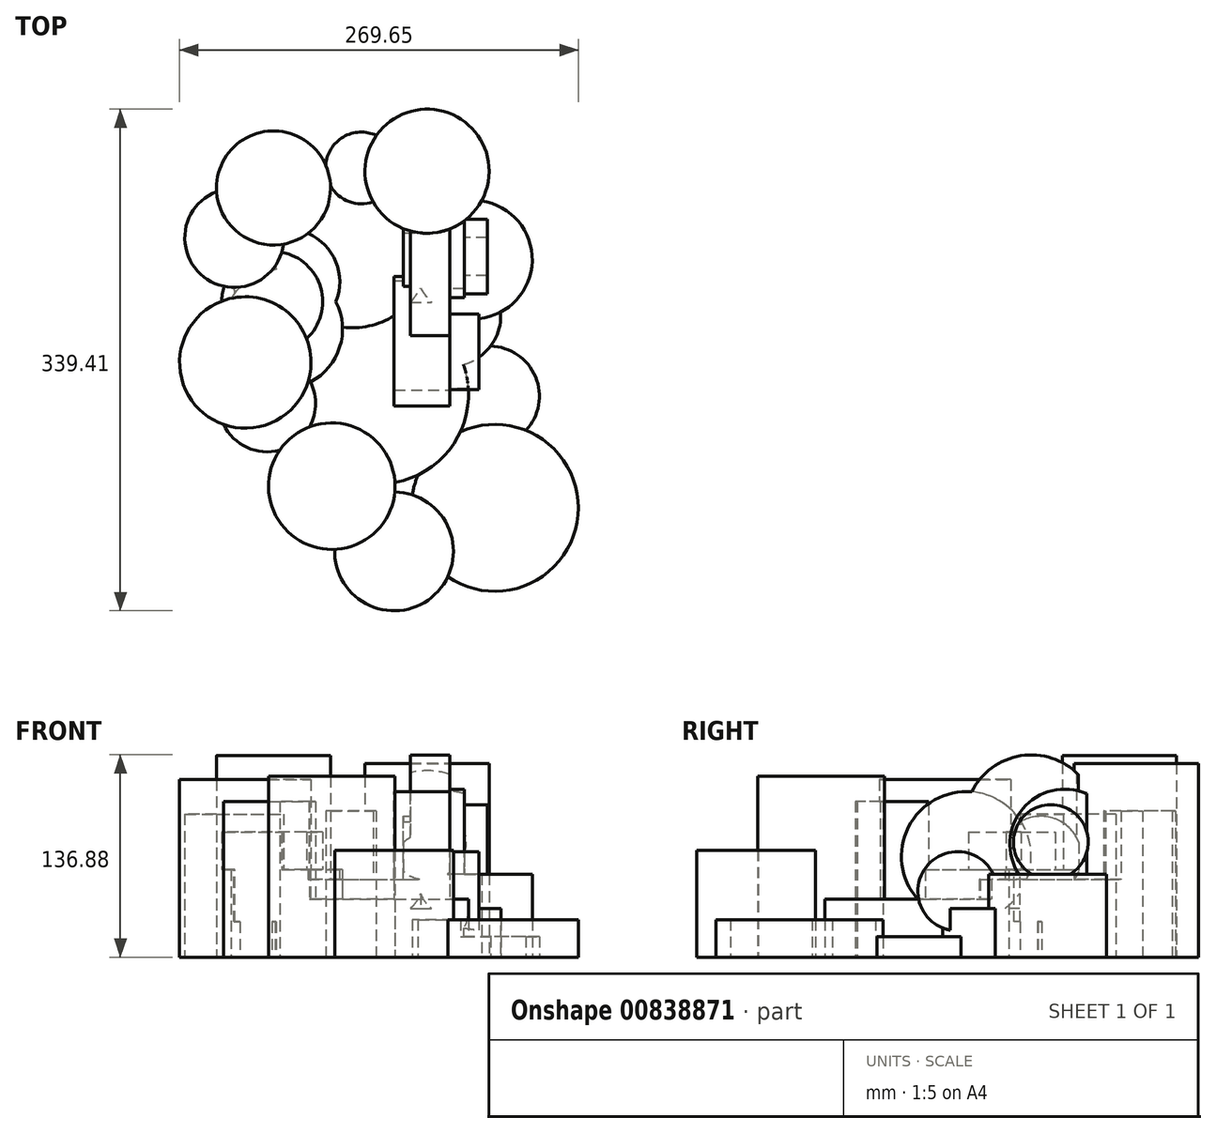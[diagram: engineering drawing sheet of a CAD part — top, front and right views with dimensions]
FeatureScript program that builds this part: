
annotation { "Feature Type Name" : "Feature", "Feature Type Description" : "" }
export const myFeature = defineFeature(function(context is Context, id is Id, definition is map)
    precondition{}
    {
        {
            var Q0;
            Q0=qCreatedBy(makeId("Top.planeOp"),FACE);
            var sketch = newSketch(context, id + "F0", { "sketchPlane" : qUnion([Q0])});
            skCircle(sketch, "E0", {"center": v(0, -74.76) * mm, "radius": 34.52 * mm});
            skSolve(sketch);
        }
        {
            var Q0;
            Q0 = qSketchRegion(id + "F0", true);
            extrude(context, id + "F1", {"entities" : qUnion([Q0]), "depth" : 33.02 * mm, "offsetDistance" : 25.4 * mm});
        }
        {
            var Q0;
            Q0=qCreatedBy(makeId("Right.planeOp"),FACE);
            var sketch = newSketch(context, id + "F2", { "sketchPlane" : qUnion([Q0])});
            skCircle(sketch, "E1", {"center": v(-92.09, 68.15) * mm, "radius": 43.86 * mm});
            skSolve(sketch);
        }
        {
            var Q0;
            Q0 = qSketchRegion(id + "F2", true);
            extrude(context, id + "F3", {"entities" : qUnion([Q0]), "operationType" : NewBodyOperationType.ADD, "oppositeDirection" : true, "depth" : 37.6 * mm, "offsetDistance" : 25.4 * mm});
        }
        {
            var Q0;
            Q0=qCreatedBy(makeId("Top.planeOp"),FACE);
            var sketch = newSketch(context, id + "F4", { "sketchPlane" : qUnion([Q0])});
            skCircle(sketch, "E2", {"center": v(-47.76, -128.19) * mm, "radius": 60.52 * mm});
            skSolve(sketch);
        }
        {
            var Q0;
            Q0 = qSketchRegion(id + "F4", true);
            extrude(context, id + "F5", {"entities" : qUnion([Q0]), "operationType" : NewBodyOperationType.ADD, "depth" : 25.4 * mm, "offsetDistance" : 25.4 * mm});
        }
        {
            var Q0;
            Q0=qCreatedBy(makeId("Top.planeOp"),FACE);
            var sketch = newSketch(context, id + "F6", { "sketchPlane" : qUnion([Q0])});
            skCircle(sketch, "E3", {"center": v(26.84, -129.33) * mm, "radius": 33.81 * mm});
            skSolve(sketch);
        }
        {
            var Q0;
            Q0 = qSketchRegion(id + "F6", true);
            var Q1;
            Q1=makeQuery(id+"F5.opExtrude","CAP_FACE",FACE,{"disambiguationData":[OSD([sQuery(id+"F4.wireOp",EDGE,"E2")])],"isStart":false});
            extrude(context, id + "F7", {"entities" : qUnion([Q0, Q1]), "operationType" : NewBodyOperationType.ADD, "depth" : 13.97 * mm, "offsetDistance" : 25.4 * mm});
        }
        {
            var Q0;
            Q0=qCreatedBy(makeId("Top.planeOp"),FACE);
            var sketch = newSketch(context, id + "F8", { "sketchPlane" : qUnion([Q0])});
            skCircle(sketch, "E4", {"center": v(-65.95, -29.9) * mm, "radius": 53.24 * mm});
            skSolve(sketch);
        }
        {
            var Q0;
            Q0 = qSketchRegion(id + "F8", true);
            extrude(context, id + "F9", {"entities" : qUnion([Q0]), "operationType" : NewBodyOperationType.ADD, "depth" : 52.58 * mm, "offsetDistance" : 25.4 * mm});
        }
        {
            var Q0;
            Q0=qCreatedBy(makeId("Top.planeOp"),FACE);
            var sketch = newSketch(context, id + "F10", { "sketchPlane" : qUnion([Q0])});
            skCircle(sketch, "E5", {"center": v(-113, -83.9) * mm, "radius": 40.49 * mm});
            skSolve(sketch);
        }
        {
            var Q0;
            Q0 = qSketchRegion(id + "F10", true);
            extrude(context, id + "F11", {"entities" : qUnion([Q0]), "operationType" : NewBodyOperationType.ADD, "depth" : 59.18 * mm, "offsetDistance" : 25.4 * mm});
        }
        {
            var Q0;
            Q0=qCreatedBy(makeId("Top.planeOp"),FACE);
            var sketch = newSketch(context, id + "F12", { "sketchPlane" : qUnion([Q0])});
            skCircle(sketch, "E6", {"center": v(-145.69, -22.25) * mm, "radius": 33.52 * mm});
            skSolve(sketch);
        }
        {
            var Q0;
            Q0 = qSketchRegion(id + "F12", true);
            extrude(context, id + "F13", {"entities" : qUnion([Q0]), "operationType" : NewBodyOperationType.ADD, "depth" : 96.77 * mm, "offsetDistance" : 25.4 * mm});
        }
        {
            var Q0;
            Q0=qCreatedBy(makeId("Top.planeOp"),FACE);
            var sketch = newSketch(context, id + "F14", { "sketchPlane" : qUnion([Q0])});
            skCircle(sketch, "E7", {"center": v(15.66, -36.96) * mm, "radius": 40.14 * mm});
            skSolve(sketch);
        }
        {
            var Q0;
            Q0 = qSketchRegion(id + "F14", true);
            extrude(context, id + "F15", {"entities" : qUnion([Q0]), "operationType" : NewBodyOperationType.ADD, "depth" : 56.13 * mm, "offsetDistance" : 25.4 * mm});
        }
        {
            var Q0;
            Q0=qCreatedBy(makeId("Right.planeOp"),FACE);
            var sketch = newSketch(context, id + "F16", { "sketchPlane" : qUnion([Q0])});
            skCircle(sketch, "E8", {"center": v(-48.2, 92.07) * mm, "radius": 44.8 * mm});
            skSolve(sketch);
        }
        {
            var Q0;
            Q0 = qSketchRegion(id + "F16", true);
            extrude(context, id + "F17", {"entities" : qUnion([Q0]), "operationType" : NewBodyOperationType.ADD, "oppositeDirection" : true, "depth" : 26.67 * mm, "offsetDistance" : 25.4 * mm});
        }
        {
            var Q0;
            Q0=makeQuery(id+"F11.opExtrude","CAP_FACE",FACE,{"disambiguationData":[OSD([sQuery(id+"F10.wireOp",EDGE,"E5")])],"isStart":false});
            var sketch = newSketch(context, id + "F18", { "sketchPlane" : qUnion([Q0])});
            skCircle(sketch, "E9", {"center": v(-110.3, -52.08) * mm, "radius": 35.94 * mm});
            skSolve(sketch);
        }
        {
            var Q0;
            Q0 = qSketchRegion(id + "F18", true);
            extrude(context, id + "F19", {"entities" : qUnion([Q0]), "operationType" : NewBodyOperationType.ADD, "oppositeDirection" : true, "depth" : 35.3 * mm, "offsetDistance" : 25.4 * mm});
        }
        {
            var Q0;
            Q0=makeQuery(id+"F19.boolean.opBoolean","MERGE",FACE,{"derivedFrom":[makeQuery(id+"F11.opExtrude","CAP_FACE",FACE,{"disambiguationData":[OSD([sQuery(id+"F10.wireOp",EDGE,"E5")])],"isStart":false}),makeQuery(id+"F19.opExtrude","CAP_FACE",FACE,{"disambiguationData":[OSD([sQuery(id+"F18.wireOp",EDGE,"E9")])],"isStart":true})]});
            var sketch = newSketch(context, id + "F20", { "sketchPlane" : qUnion([Q0])});
            skCircle(sketch, "E10", {"center": v(-120.06, -65.46) * mm, "radius": 34.14 * mm});
            skPoint(sketch, "E10.centerSnap0", {"position": v(-120.06, -43.85) * mm});
            skSolve(sketch);
        }
        {
            var Q0;
            Q0 = qSketchRegion(id + "F20", true);
            extrude(context, id + "F21", {"entities" : qUnion([Q0]), "operationType" : NewBodyOperationType.ADD, "depth" : 25.4 * mm, "offsetDistance" : 25.4 * mm});
        }
        {
            var Q0;
            Q0=qCreatedBy(makeId("Top.planeOp"),FACE);
            var sketch = newSketch(context, id + "F22", { "sketchPlane" : qUnion([Q0])});
            skCircle(sketch, "E11", {"center": v(-123.47, -134.29) * mm, "radius": 32.73 * mm});
            skSolve(sketch);
        }
        {
            var Q0;
            Q0 = qSketchRegion(id + "F22", true);
            extrude(context, id + "F23", {"entities" : qUnion([Q0]), "operationType" : NewBodyOperationType.ADD, "depth" : 105.4 * mm, "offsetDistance" : 25.4 * mm});
        }
        {
            var Q0;
            Q0=qCreatedBy(makeId("Top.planeOp"),FACE);
            var sketch = newSketch(context, id + "F24", { "sketchPlane" : qUnion([Q0])});
            skCircle(sketch, "E12", {"center": v(-79.76, -190.25) * mm, "radius": 42.8 * mm});
            skSolve(sketch);
        }
        {
            var Q0;
            Q0 = qSketchRegion(id + "F24", true);
            extrude(context, id + "F25", {"entities" : qUnion([Q0]), "operationType" : NewBodyOperationType.ADD, "depth" : 122.43 * mm, "offsetDistance" : 25.4 * mm});
        }
        {
            var Q0;
            Q0=qCreatedBy(makeId("Top.planeOp"),FACE);
            var sketch = newSketch(context, id + "F26", { "sketchPlane" : qUnion([Q0])});
            skCircle(sketch, "E13", {"center": v(30.49, -204.93) * mm, "radius": 56.45 * mm});
            skSolve(sketch);
        }
        {
            var Q0;
            Q0 = qSketchRegion(id + "F26", true);
            extrude(context, id + "F27", {"entities" : qUnion([Q0]), "operationType" : NewBodyOperationType.ADD, "depth" : 25.4 * mm, "offsetDistance" : 25.4 * mm});
        }
        {
            var Q0;
            Q0=qCreatedBy(makeId("Top.planeOp"),FACE);
            var sketch = newSketch(context, id + "F28", { "sketchPlane" : qUnion([Q0])});
            skCircle(sketch, "E14", {"center": v(-37.66, -234.4) * mm, "radius": 40.17 * mm});
            skSolve(sketch);
        }
        {
            var Q0;
            Q0 = qSketchRegion(id + "F28", true);
            extrude(context, id + "F29", {"entities" : qUnion([Q0]), "operationType" : NewBodyOperationType.ADD, "depth" : 72.39 * mm, "offsetDistance" : 25.4 * mm});
        }
        {
            var Q0;
            Q0=qCreatedBy(makeId("Top.planeOp"),FACE);
            var sketch = newSketch(context, id + "F30", { "sketchPlane" : qUnion([Q0])});
            skCircle(sketch, "E15", {"center": v(-119.2, 11.54) * mm, "radius": 38.58 * mm});
            skSolve(sketch);
        }
        {
            var Q0;
            Q0 = qSketchRegion(id + "F30", true);
            extrude(context, id + "F31", {"entities" : qUnion([Q0]), "operationType" : NewBodyOperationType.ADD, "depth" : 136.4 * mm, "offsetDistance" : 25.4 * mm});
        }
        {
            var Q0;
            Q0=qCreatedBy(makeId("Top.planeOp"),FACE);
            var sketch = newSketch(context, id + "F32", { "sketchPlane" : qUnion([Q0])});
            skCircle(sketch, "E16", {"center": v(-138.26, -106.57) * mm, "radius": 44.45 * mm});
            skSolve(sketch);
        }
        {
            var Q0;
            Q0 = qSketchRegion(id + "F32", true);
            extrude(context, id + "F33", {"entities" : qUnion([Q0]), "operationType" : NewBodyOperationType.ADD, "depth" : 120.14 * mm, "offsetDistance" : 25.4 * mm});
        }
        {
            var Q0;
            Q0=qCreatedBy(makeId("Top.planeOp"),FACE);
            var sketch = newSketch(context, id + "F34", { "sketchPlane" : qUnion([Q0])});
            skCircle(sketch, "E17", {"center": v(-15.33, 22.86) * mm, "radius": 41.98 * mm});
            skSolve(sketch);
        }
        {
            var Q0;
            Q0 = qSketchRegion(id + "F34", true);
            extrude(context, id + "F35", {"entities" : qUnion([Q0]), "operationType" : NewBodyOperationType.ADD, "depth" : 131.06 * mm, "offsetDistance" : 25.4 * mm});
        }
        {
            var Q0;
            Q0=qCreatedBy(makeId("Top.planeOp"),FACE);
            var sketch = newSketch(context, id + "F36", { "sketchPlane" : qUnion([Q0])});
            skCircle(sketch, "E18", {"center": v(-59.75, 25.05) * mm, "radius": 24.26 * mm});
            skSolve(sketch);
        }
        {
            var Q0;
            Q0 = qSketchRegion(id + "F36", true);
            extrude(context, id + "F37", {"entities" : qUnion([Q0]), "operationType" : NewBodyOperationType.ADD, "depth" : 99.06 * mm, "offsetDistance" : 25.4 * mm});
        }
        {
            var Q0;
            Q0=qCreatedBy(makeId("Right.planeOp"),FACE);
            var sketch = newSketch(context, id + "F38", { "sketchPlane" : qUnion([Q0])});
            skCircle(sketch, "E19", {"center": v(-41.64, 67.87) * mm, "radius": 27.45 * mm});
            skSolve(sketch);
        }
        {
            var Q0;
            Q0 = qSketchRegion(id + "F38", true);
            extrude(context, id + "F39", {"entities" : qUnion([Q0]), "operationType" : NewBodyOperationType.ADD, "oppositeDirection" : true, "depth" : 31.24 * mm, "offsetDistance" : 25.4 * mm});
        }
        {
            var Q0;
            Q0=makeQuery(id+"F39.boolean.opBoolean","MERGE",FACE,{"derivedFrom":[makeQuery(id+"F17.boolean.opBoolean","MERGE",FACE,{"derivedFrom":[makeQuery(id+"F3.opExtrude","CAP_FACE",FACE,{"disambiguationData":[OSD([sQuery(id+"F2.wireOp",EDGE,"E1")])],"isStart":true}),makeQuery(id+"F17.opExtrude","CAP_FACE",FACE,{"disambiguationData":[OSD([sQuery(id+"F16.wireOp",EDGE,"E8")])],"isStart":true})]}),makeQuery(id+"F39.opExtrude","CAP_FACE",FACE,{"disambiguationData":[OSD([sQuery(id+"F38.wireOp",EDGE,"E19")])],"isStart":true})]});
            var sketch = newSketch(context, id + "F40", { "sketchPlane" : qUnion([Q0])});
            skCircle(sketch, "E20", {"center": v(-34.93, 77.87) * mm, "radius": 25.3 * mm});
            skSolve(sketch);
        }
        {
            var Q0;
            Q0 = qSketchRegion(id + "F40", true);
            extrude(context, id + "F41", {"entities" : qUnion([Q0]), "operationType" : NewBodyOperationType.ADD, "depth" : 25.4 * mm, "offsetDistance" : 25.4 * mm});
        }
        {
            var Q0;
            {var subQ1=sQuery(id+"F0.wireOp",EDGE,"E0");var subQ2=sQuery(id+"F16.wireOp",EDGE,"E8");var subQ3=sQuery(id+"F2.wireOp",EDGE,"E1");Q0=makeQuery(id+"F41.boolean.opBoolean","SPLIT",FACE,{"disambiguationData":[TD([makeQuery(id+"F1.opExtrude","CAP_FACE",FACE,{"disambiguationData":[OSD([subQ1])],"isStart":false})])],"derivedFrom":makeQuery(id+"F39.boolean.opBoolean","MERGE",FACE,{"derivedFrom":[makeQuery(id+"F17.boolean.opBoolean","MERGE",FACE,{"derivedFrom":[makeQuery(id+"F3.opExtrude","CAP_FACE",FACE,{"disambiguationData":[OSD([subQ3])],"isStart":true}),makeQuery(id+"F17.opExtrude","CAP_FACE",FACE,{"disambiguationData":[OSD([subQ2])],"isStart":true})]}),makeQuery(id+"F39.opExtrude","CAP_FACE",FACE,{"disambiguationData":[OSD([sQuery(id+"F38.wireOp",EDGE,"E19")])],"isStart":true})]})});}
            var sketch = newSketch(context, id + "F42", { "sketchPlane" : qUnion([Q0])});
            skCircle(sketch, "E21", {"center": v(-25.52, 76.55) * mm, "radius": 37.1 * mm});
            skSolve(sketch);
        }
        {
            var Q0;
            Q0 = qSketchRegion(id + "F42", true);
            extrude(context, id + "F43", {"entities" : qUnion([Q0]), "operationType" : NewBodyOperationType.ADD, "depth" : 9.9 * mm, "offsetDistance" : 25.4 * mm});
        }
        {
            var Q0;
            {var subQ1=sQuery(id+"F0.wireOp",EDGE,"E0");var subQ2=sQuery(id+"F16.wireOp",EDGE,"E8");var subQ3=sQuery(id+"F2.wireOp",EDGE,"E1");Q0=makeQuery(id+"F41.boolean.opBoolean","SPLIT",FACE,{"disambiguationData":[TD([makeQuery(id+"F1.opExtrude","CAP_FACE",FACE,{"disambiguationData":[OSD([subQ1])],"isStart":false})])],"derivedFrom":makeQuery(id+"F39.boolean.opBoolean","MERGE",FACE,{"derivedFrom":[makeQuery(id+"F17.boolean.opBoolean","MERGE",FACE,{"derivedFrom":[makeQuery(id+"F3.opExtrude","CAP_FACE",FACE,{"disambiguationData":[OSD([subQ3])],"isStart":true}),makeQuery(id+"F17.opExtrude","CAP_FACE",FACE,{"disambiguationData":[OSD([subQ2])],"isStart":true})]}),makeQuery(id+"F39.opExtrude","CAP_FACE",FACE,{"disambiguationData":[OSD([sQuery(id+"F38.wireOp",EDGE,"E19")])],"isStart":true})]})});}
            var sketch = newSketch(context, id + "F44", { "sketchPlane" : qUnion([Q0])});
            skCircle(sketch, "E22", {"center": v(-98.08, 44.58) * mm, "radius": 26.79 * mm});
            skPoint(sketch, "E22.centerSnap0", {"position": v(-73.91, 44.58) * mm});
            skSolve(sketch);
        }
        {
            var Q0;
            Q0 = qSketchRegion(id + "F44", true);
            extrude(context, id + "F45", {"entities" : qUnion([Q0]), "operationType" : NewBodyOperationType.ADD, "depth" : 19.8 * mm, "offsetDistance" : 25.4 * mm});
        }
    });
